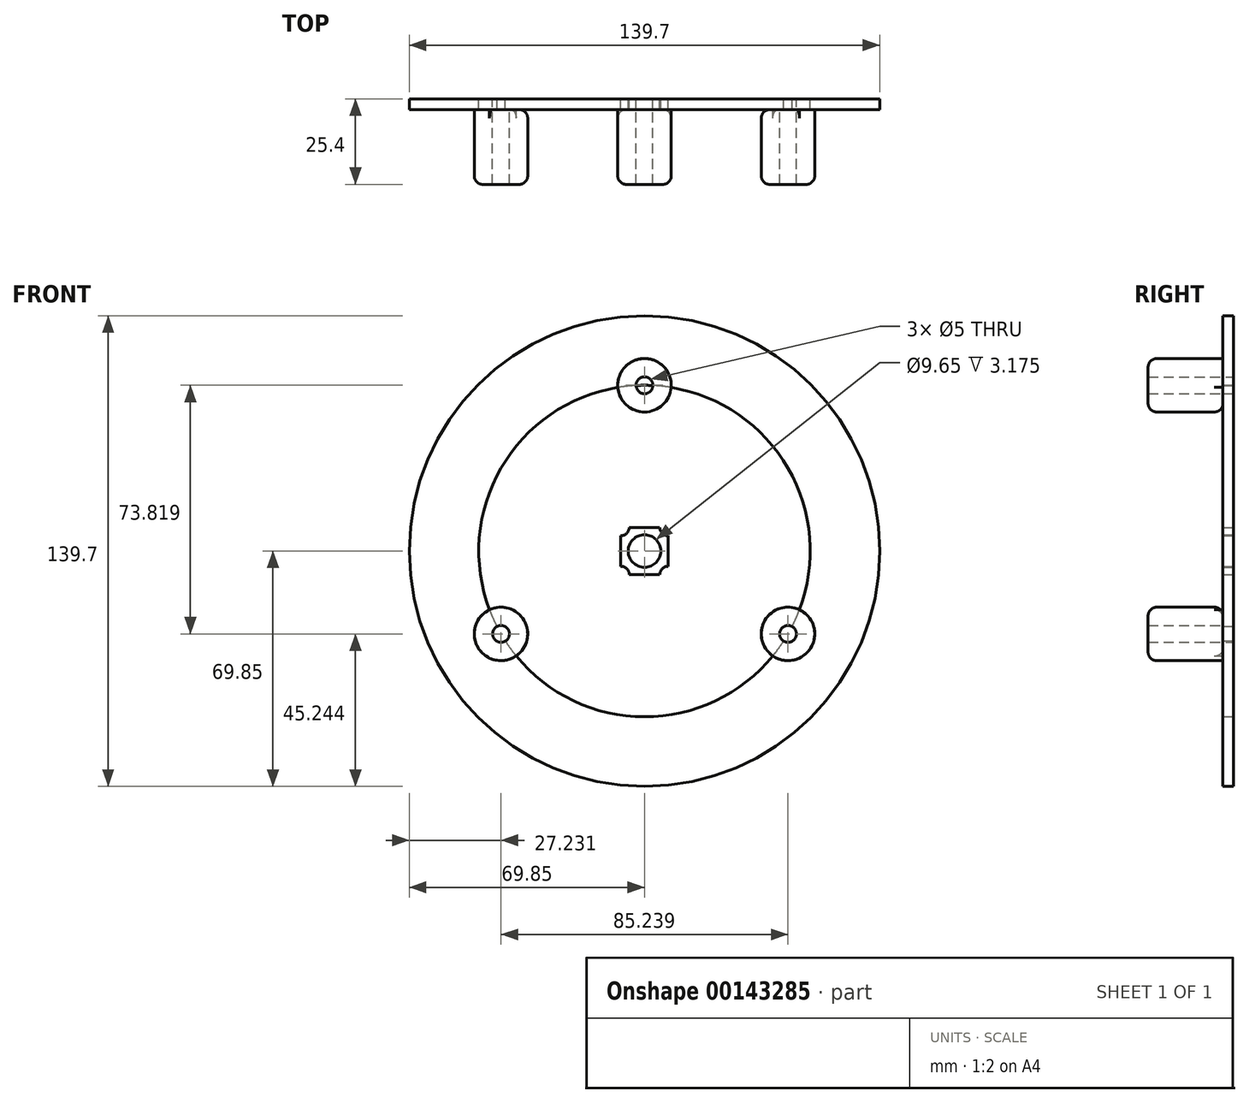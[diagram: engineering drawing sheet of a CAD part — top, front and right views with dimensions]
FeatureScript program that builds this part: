
annotation { "Feature Type Name" : "Feature", "Feature Type Description" : "" }
export const myFeature = defineFeature(function(context is Context, id is Id, definition is map)
    precondition{}
    {
        {
            var Q0;
            Q0=qCreatedBy(makeId("Front.planeOp"),FACE);
            var sketch = newSketch(context, id + "F0", { "sketchPlane" : qUnion([Q0])});
            skCircle(sketch, "E0", {"center": v(0, 0) * mm, "radius": 69.85 * mm});
            skCircle(sketch, "E1", {"center": v(0, 0) * mm, "radius": 49.21 * mm});
            skLineSegment(sketch, "E2.bottom", {"start": v(7.04, 7.04) * mm, "end": v(-7.04, 7.04) * mm});
            skLineSegment(sketch, "E2.top", {"start": v(7.04, -7.04) * mm, "end": v(-7.04, -7.04) * mm});
            skLineSegment(sketch, "E2.left", {"start": v(7.04, 7.04) * mm, "end": v(7.04, -7.04) * mm});
            skLineSegment(sketch, "E2.right", {"start": v(-7.04, 7.04) * mm, "end": v(-7.04, -7.04) * mm});
            skCircle(sketch, "E3", {"center": v(7.04, 7.04) * mm, "radius": 2.5 * mm});
            skCircle(sketch, "E4", {"center": v(7.04, -7.04) * mm, "radius": 2.5 * mm});
            skCircle(sketch, "E5", {"center": v(-7.04, -7.04) * mm, "radius": 2.5 * mm});
            skCircle(sketch, "E6", {"center": v(-7.04, 7.04) * mm, "radius": 2.5 * mm});
            skCircle(sketch, "E7", {"center": v(0, 49.21) * mm, "radius": 2.5 * mm});
            skCircle(sketch, "E8.1.0", {"center": v(-42.62, -24.6) * mm, "radius": 2.5 * mm});
            skCircle(sketch, "E8.2.0", {"center": v(42.62, -24.6) * mm, "radius": 2.5 * mm});
            skCircle(sketch, "E9", {"center": v(0, 0) * mm, "radius": 4.83 * mm});
            skSolve(sketch);
        }
        {
            var Q0;
            Q0=qSketchRegion(id+"F0",true);
            var Q1;
            {var subQ11=sQuery(id+"F0.wireOp",EDGE,"E7");var subQ12=sQuery(id+"F0.wireOp",EDGE,"E1");var subQ13=makeQuery(id+"F0.imprint","INTERSECT",VERTEX,{"disambiguationData":[OD(0.0)],"derivedFrom":[subQ12,subQ11]});Q1=makeQuery(id+"F0.imprint","IMPRINT",FACE,{"disambiguationData":[TD([[makeQuery(id+"F0.imprint","IMPRINT",EDGE,{"disambiguationData":[TD([[subQ13,-1.0]])],"derivedFrom":subQ12}),1.0]])]});}
            var Q2;
            {var subQ5=sQuery(id+"F0.wireOp",EDGE,"E3");var subQ13=sQuery(id+"F0.wireOp",EDGE,"E2.bottom");var subQ14=makeQuery(id+"F0.imprint","INTERSECT",VERTEX,{"derivedFrom":[subQ13,subQ5]});Q2=makeQuery(id+"F0.imprint","IMPRINT",FACE,{"disambiguationData":[TD([[makeQuery(id+"F0.imprint","IMPRINT",EDGE,{"disambiguationData":[TD([[subQ14,-1.0]])],"derivedFrom":subQ13}),1.0]])]});}
            extrude(context, id + "F1", {"entities" : qUnion([Q0, Q1, Q2]), "depth" : 3.17 * mm});
        }
        {
            var Q0;
            Q0=makeQuery(id+"F1.opExtrude","CAP_FACE",FACE,{"disambiguationData":[OSD([sQuery(id+"F0.wireOp",EDGE,"E0"),sQuery(id+"F0.wireOp",EDGE,"E3"),sQuery(id+"F0.wireOp",EDGE,"E4"),sQuery(id+"F0.wireOp",EDGE,"E5"),sQuery(id+"F0.wireOp",EDGE,"E6"),sQuery(id+"F0.wireOp",EDGE,"E7"),sQuery(id+"F0.wireOp",EDGE,"E8.1.0"),sQuery(id+"F0.wireOp",EDGE,"E8.2.0"),sQuery(id+"F0.wireOp",EDGE,"E9")])],"isStart":false});
            var sketch = newSketch(context, id + "F2", { "sketchPlane" : qUnion([Q0])});
            skCircle(sketch, "E10", {"center": v(0, 49.21) * mm, "radius": 2.5 * mm});
            skCircle(sketch, "E11", {"center": v(0, 49.21) * mm, "radius": 7.94 * mm});
            skCircle(sketch, "E12", {"center": v(-42.62, -24.6) * mm, "radius": 7.94 * mm});
            skCircle(sketch, "E13", {"center": v(-42.62, -24.6) * mm, "radius": 2.5 * mm});
            skCircle(sketch, "E14", {"center": v(42.62, -24.6) * mm, "radius": 7.94 * mm});
            skCircle(sketch, "E15", {"center": v(42.62, -24.6) * mm, "radius": 2.5 * mm});
            skSolve(sketch);
        }
        {
            var Q0;
            Q0 = qSketchRegion(id + "F2", true);
            extrude(context, id + "F3", {"entities" : qUnion([Q0]), "operationType" : NewBodyOperationType.ADD, "depth" : 22.22 * mm, "offsetDistance" : 25.4 * mm});
        }
        {
            var Q0;
            Q0=makeQuery(id+"F3.opExtrude","CAP_EDGE",EDGE,{"disambiguationData":[OSD([sQuery(id+"F2.wireOp",EDGE,"E11")])],"isStart":true});
            var Q1;
            Q1=makeQuery(id+"F3.opExtrude","CAP_EDGE",EDGE,{"disambiguationData":[OSD([sQuery(id+"F2.wireOp",EDGE,"E14")])],"isStart":true});
            var Q2;
            Q2=makeQuery(id+"F3.opExtrude","CAP_EDGE",EDGE,{"disambiguationData":[OSD([sQuery(id+"F2.wireOp",EDGE,"E12")])],"isStart":true});
            var Q3;
            Q3=makeQuery(id+"F3.opExtrude","CAP_EDGE",EDGE,{"disambiguationData":[OSD([sQuery(id+"F2.wireOp",EDGE,"E11")])],"isStart":false});
            var Q4;
            Q4=makeQuery(id+"F3.opExtrude","CAP_EDGE",EDGE,{"disambiguationData":[OSD([sQuery(id+"F2.wireOp",EDGE,"E14")])],"isStart":false});
            var Q5;
            Q5=makeQuery(id+"F3.opExtrude","CAP_EDGE",EDGE,{"disambiguationData":[OSD([sQuery(id+"F2.wireOp",EDGE,"E12")])],"isStart":false});
            fillet(context, id + "F4", {"entities" : qUnion([Q0, Q1, Q2, Q3, Q4, Q5]), "radius" : 2.54 * mm, "tangentPropagation" : true, "allowEdgeOverflow" : false});
        }
    });
